FCSTD DOCUMENT  (FreeCAD 0.18R16110 (Git))
Label: 4sideP
License: All rights reserved
LicenseURL: http://en.wikipedia.org/wiki/All_rights_reserved
objects: Sketcher::SketchObject×1
note: 1 computed .brp shape members not serialized (recipe doc carries the construction recipe); baked Part::Feature solids carry a one-line shape summary decoded from their .brp

FEATURE [Sketcher::SketchObject] Sketch
  sketch-geometry (9):
    g0: LineSegment StartX=-500 StartY=500 StartZ=0 EndX=500 EndY=500 EndZ=0
    g1: LineSegment StartX=500 StartY=500 StartZ=0 EndX=500 EndY=-500 EndZ=0
    g2: LineSegment StartX=500 StartY=-500 StartZ=0 EndX=-500 EndY=-500 EndZ=0
    g3: LineSegment StartX=-500 StartY=-500 StartZ=0 EndX=-500 EndY=500 EndZ=0
    g4: Circle [constr] CenterX=0 CenterY=0 CenterZ=0 NormalX=0 NormalY=0 NormalZ=1 AngleXU=0 Radius=255
    g5: LineSegment StartX=-500 StartY=500 StartZ=0 EndX=-28.6039 EndY=253.391 EndZ=0
    g6: LineSegment StartX=500 StartY=500 StartZ=0 EndX=252.945 EndY=32.3085 EndZ=0
    g7: LineSegment StartX=500 StartY=-500 StartZ=0 EndX=29.2779 EndY=-252.72 EndZ=0
    g8: LineSegment StartX=-500 StartY=-500 StartZ=0 EndX=-254.871 EndY=-31.8528 EndZ=0
  constraints (20):
    c: Coincident(g0,g1)
    c: Coincident(g1,g2)
    c: Coincident(g2,g3)
    c: Coincident(g3,g0)
    c: Horizontal(g0)
    c: Horizontal(g2)
    c: Vertical(g1)
    c: Vertical(g3)
    c: DistanceY(g0) = 500
    c: DistanceY(g1) = -500
    c: DistanceX(g0) = 500
    c: DistanceX(g0) = -500
    c: PointOnObject(g6,g4)
    c: PointOnObject(g5,g4)
    c: Coincident(g4,g-1)
    c: Coincident(g5,g0)
    c: Coincident(g6,g0)
    c: Coincident(g7,g1)
    c: Coincident(g8,g2)
    c: Radius(g4) = 255
